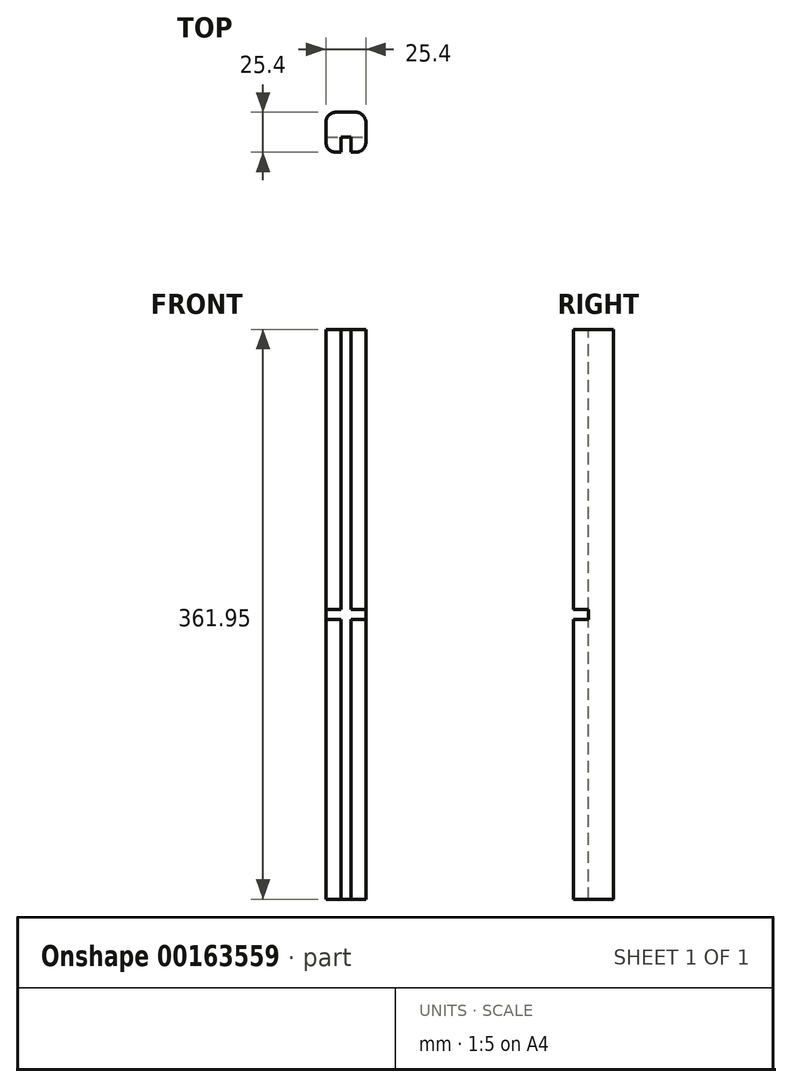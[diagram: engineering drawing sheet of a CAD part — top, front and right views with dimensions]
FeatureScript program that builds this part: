
annotation { "Feature Type Name" : "Feature", "Feature Type Description" : "" }
export const myFeature = defineFeature(function(context is Context, id is Id, definition is map)
    precondition{}
    {
        {
            var Q0;
            Q0=qCreatedBy(makeId("Top.planeOp"),FACE);
            var sketch = newSketch(context, id + "F0", { "sketchPlane" : qUnion([Q0])});
            skLineSegment(sketch, "E0.bottom", {"start": v(6.35, 12.7) * mm, "end": v(-6.35, 12.7) * mm});
            skLineSegment(sketch, "E0.top", {"start": v(6.35, -12.7) * mm, "end": v(-6.35, -12.7) * mm});
            skLineSegment(sketch, "E0.left", {"start": v(12.7, 6.35) * mm, "end": v(12.7, -6.35) * mm});
            skLineSegment(sketch, "E0.right", {"start": v(-12.7, 6.35) * mm, "end": v(-12.7, -6.35) * mm});
            skPoint(sketch, "E0.middle", {"position": v(0, 0) * mm});
            skPoint(sketch, "E1.visualSharp", {"position": v(-12.7, 12.7) * mm});
            skArc(sketch, "E1.filletArc", {"start": v(-6.35, 12.7) * mm, "mid": v(-10.84, 10.84) * mm, "end": v(-12.7, 6.35) * mm});
            skPoint(sketch, "E2.visualSharp", {"position": v(-12.7, -12.7) * mm});
            skArc(sketch, "E2.filletArc", {"start": v(-12.7, -6.35) * mm, "mid": v(-10.84, -10.84) * mm, "end": v(-6.35, -12.7) * mm});
            skPoint(sketch, "E3.visualSharp", {"position": v(12.7, -12.7) * mm});
            skArc(sketch, "E3.filletArc", {"start": v(6.35, -12.7) * mm, "mid": v(10.84, -10.84) * mm, "end": v(12.7, -6.35) * mm});
            skPoint(sketch, "E4.visualSharp", {"position": v(12.7, 12.7) * mm});
            skArc(sketch, "E4.filletArc", {"start": v(12.7, 6.35) * mm, "mid": v(10.84, 10.84) * mm, "end": v(6.35, 12.7) * mm});
            skSolve(sketch);
        }
        {
            var Q0;
            Q0=qSketchRegion(id+"F0",true);
            extrude(context, id + "F1", {"entities" : qUnion([Q0]), "depth" : 361.95 * mm, "offsetDistance" : 25.4 * mm});
        }
        {
            var Q0;
            Q0=makeQuery(id+"F1.opExtrude","SWEPT_FACE",FACE,{"disambiguationData":[OSD([sQuery(id+"F0.wireOp",EDGE,"E0.top")])]});
            var sketch = newSketch(context, id + "F2", { "sketchPlane" : qUnion([Q0])});
            skPoint(sketch, "E5.orphan", {"position": v(6.35, 180.98) * mm});
            skLineSegment(sketch, "E6.bottom", {"start": v(-12.7, 177.8) * mm, "end": v(12.7, 177.8) * mm});
            skLineSegment(sketch, "E6.top", {"start": v(-12.7, 184.15) * mm, "end": v(12.7, 184.15) * mm});
            skLineSegment(sketch, "E6.left", {"start": v(-12.7, 177.8) * mm, "end": v(-12.7, 184.15) * mm});
            skLineSegment(sketch, "E6.right", {"start": v(12.7, 177.8) * mm, "end": v(12.7, 184.15) * mm});
            skPoint(sketch, "E6.middle", {"position": v(0, 180.98) * mm});
            skLineSegment(sketch, "E7.bottom", {"start": v(3.17, 0) * mm, "end": v(-3.18, 0) * mm});
            skLineSegment(sketch, "E7.top", {"start": v(3.17, 361.95) * mm, "end": v(-3.18, 361.95) * mm});
            skLineSegment(sketch, "E7.left", {"start": v(3.17, 0) * mm, "end": v(3.17, 361.95) * mm});
            skLineSegment(sketch, "E7.right", {"start": v(-3.18, 0) * mm, "end": v(-3.18, 361.95) * mm});
            skSolve(sketch);
        }
        {
            var Q0;
            {var subQ0=sQuery(id+"F2.wireOp",EDGE,"E6.bottom");var subQ1=sQuery(id+"F0.wireOp",EDGE,"E0.top");var subQ2=makeQuery(id+"F1.opExtrude","SWEPT_EDGE",EDGE,{"disambiguationData":[OSD([subQ1,sQuery(id+"F0.wireOp",EDGE,"E2.filletArc")])]});var subQ3=makeQuery(id+"F2.imprint","INTERSECT",VERTEX,{"derivedFrom":[subQ2,subQ0]});Q0=makeQuery(id+"F2.imprint","IMPRINT",FACE,{"disambiguationData":[TD([[makeQuery(id+"F2.imprint","IMPRINT",EDGE,{"disambiguationData":[TD([[subQ3,-1.0]])],"derivedFrom":subQ0}),1.0]])]});}
            var Q1;
            {var subQ0=sQuery(id+"F2.wireOp",EDGE,"E6.left");Q1=makeQuery(id+"F2.imprint","IMPRINT",FACE,{"disambiguationData":[TD([[makeQuery(id+"F2.imprint","IMPRINT",EDGE,{"derivedFrom":subQ0}),-1.0]])]});}
            var Q2;
            {var subQ0=sQuery(id+"F2.wireOp",EDGE,"E6.right");Q2=makeQuery(id+"F2.imprint","IMPRINT",FACE,{"disambiguationData":[TD([[makeQuery(id+"F2.imprint","IMPRINT",EDGE,{"derivedFrom":subQ0}),1.0]])]});}
            extrude(context, id + "F3", {"entities" : qUnion([Q0, Q1, Q2]), "operationType" : NewBodyOperationType.REMOVE, "oppositeDirection" : true, "depth" : 9.52 * mm, "offsetDistance" : 25.4 * mm});
        }
        {
            var Q0;
            {var subQ5=sQuery(id+"F2.wireOp",EDGE,"E7.top");Q0=makeQuery(id+"F2.imprint","IMPRINT",FACE,{"disambiguationData":[TD([[makeQuery(id+"F2.imprint","IMPRINT",EDGE,{"derivedFrom":subQ5}),1.0]])]});}
            var Q1;
            {var subQ5=sQuery(id+"F2.wireOp",EDGE,"E7.bottom");Q1=makeQuery(id+"F2.imprint","IMPRINT",FACE,{"disambiguationData":[TD([[makeQuery(id+"F2.imprint","IMPRINT",EDGE,{"derivedFrom":subQ5}),-1.0]])]});}
            var Q2;
            {var subQ0=sQuery(id+"F2.wireOp",EDGE,"E7.right");var subQ1=sQuery(id+"F2.wireOp",EDGE,"E6.bottom");var subQ2=makeQuery(id+"F2.imprint","INTERSECT",VERTEX,{"derivedFrom":[subQ1,subQ0]});Q2=makeQuery(id+"F2.imprint","IMPRINT",FACE,{"disambiguationData":[TD([[makeQuery(id+"F2.imprint","IMPRINT",EDGE,{"disambiguationData":[TD([[subQ2,-1.0]])],"derivedFrom":subQ1}),1.0]])]});}
            extrude(context, id + "F4", {"entities" : qUnion([Q0, Q1, Q2]), "operationType" : NewBodyOperationType.REMOVE, "oppositeDirection" : true, "depth" : 9.52 * mm, "offsetDistance" : 25.4 * mm});
        }
        {
            var Q0;
            {var subQ0=sQuery(id+"F2.wireOp",EDGE,"E7.left");var subQ1=sQuery(id+"F2.wireOp",EDGE,"E6.bottom");var subQ2=makeQuery(id+"F2.imprint","INTERSECT",VERTEX,{"derivedFrom":[subQ1,subQ0]});Q0=makeQuery(id+"F2.imprint","IMPRINT",FACE,{"disambiguationData":[TD([[makeQuery(id+"F2.imprint","IMPRINT",EDGE,{"disambiguationData":[TD([[subQ2,-1.0]])],"derivedFrom":subQ0}),-1.0]])]});}
            var Q1;
            {var subQ0=sQuery(id+"F2.wireOp",EDGE,"E6.right");Q1=makeQuery(id+"F2.imprint","IMPRINT",FACE,{"disambiguationData":[TD([[makeQuery(id+"F2.imprint","IMPRINT",EDGE,{"derivedFrom":subQ0}),1.0]])]});}
            var Q2;
            {var subQ0=sQuery(id+"F2.wireOp",EDGE,"E7.right");var subQ1=sQuery(id+"F2.wireOp",EDGE,"E6.bottom");var subQ2=makeQuery(id+"F2.imprint","INTERSECT",VERTEX,{"derivedFrom":[subQ1,subQ0]});Q2=makeQuery(id+"F2.imprint","IMPRINT",FACE,{"disambiguationData":[TD([[makeQuery(id+"F2.imprint","IMPRINT",EDGE,{"disambiguationData":[TD([[subQ2,-1.0]])],"derivedFrom":subQ0}),1.0]])]});}
            var Q3;
            {var subQ0=sQuery(id+"F2.wireOp",EDGE,"E7.right");var subQ1=sQuery(id+"F2.wireOp",EDGE,"E6.bottom");var subQ2=makeQuery(id+"F2.imprint","INTERSECT",VERTEX,{"derivedFrom":[subQ1,subQ0]});Q3=makeQuery(id+"F2.imprint","IMPRINT",FACE,{"disambiguationData":[TD([[makeQuery(id+"F2.imprint","IMPRINT",EDGE,{"disambiguationData":[TD([[subQ2,-1.0]])],"derivedFrom":subQ1}),1.0]])]});}
            var Q4;
            {var subQ0=sQuery(id+"F2.wireOp",EDGE,"E6.left");Q4=makeQuery(id+"F2.imprint","IMPRINT",FACE,{"disambiguationData":[TD([[makeQuery(id+"F2.imprint","IMPRINT",EDGE,{"derivedFrom":subQ0}),-1.0]])]});}
            extrude(context, id + "F5", {"entities" : qUnion([Q0, Q1, Q2, Q3, Q4]), "operationType" : NewBodyOperationType.REMOVE, "oppositeDirection" : true, "depth" : 9.52 * mm, "offsetDistance" : 25.4 * mm});
        }
    });
